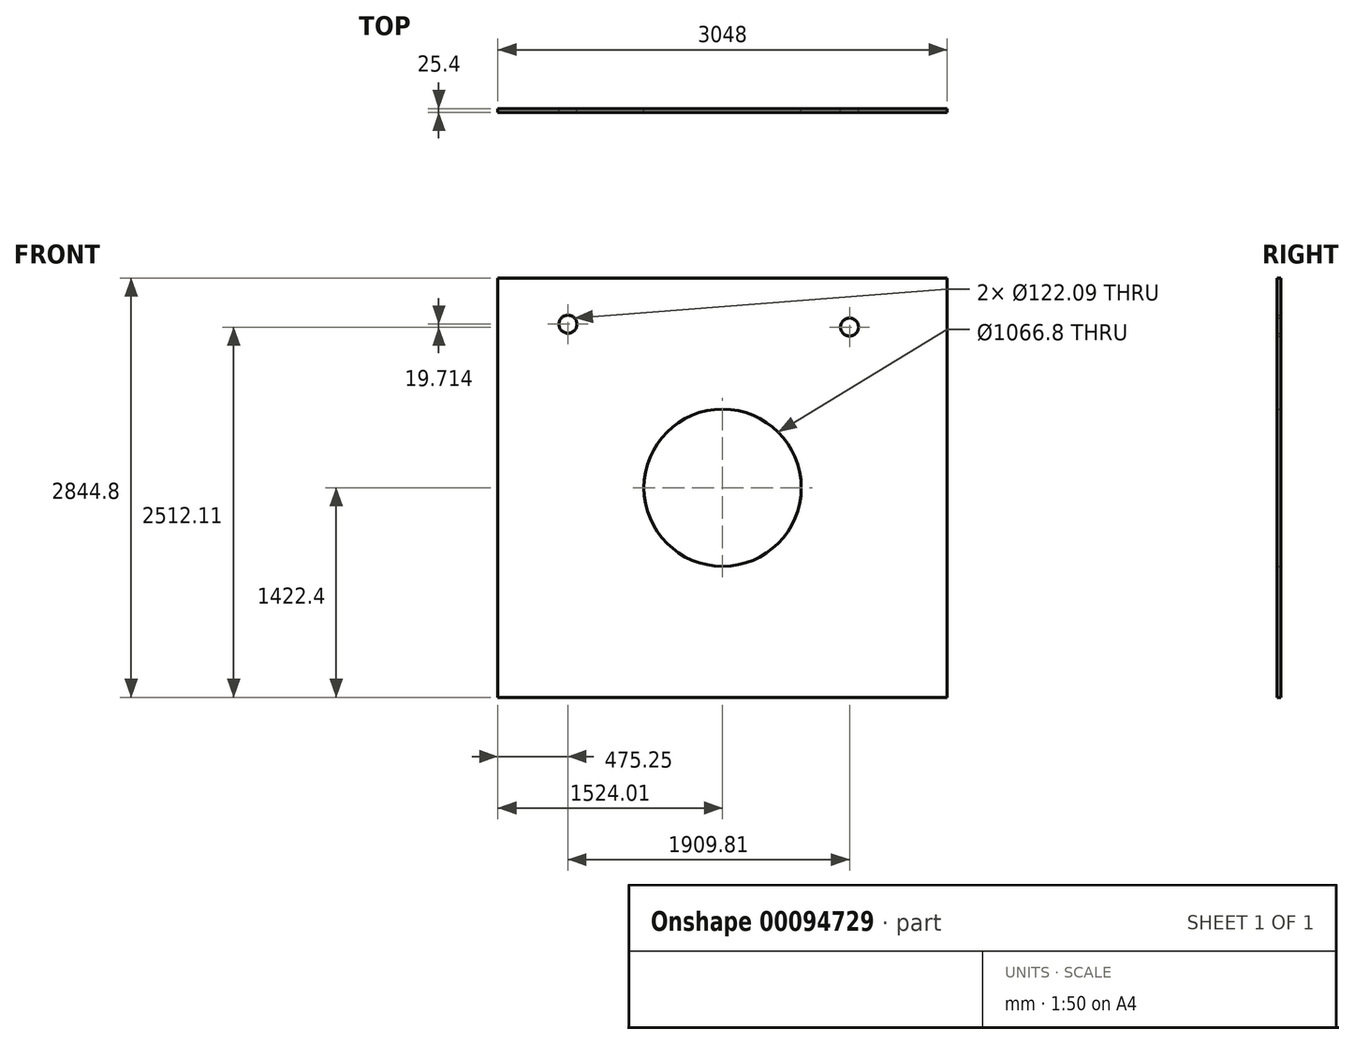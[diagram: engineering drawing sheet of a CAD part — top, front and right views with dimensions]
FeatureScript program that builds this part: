
annotation { "Feature Type Name" : "Feature", "Feature Type Description" : "" }
export const myFeature = defineFeature(function(context is Context, id is Id, definition is map)
    precondition{}
    {
        {
            var Q0;
            Q0=qCreatedBy(makeId("Front.planeOp"),FACE);
            var sketch = newSketch(context, id + "F0", { "sketchPlane" : qUnion([Q0])});
            skLineSegment(sketch, "E0.bottom", {"start": v(-1748.58, 0) * mm, "end": v(1299.42, 0) * mm});
            skLineSegment(sketch, "E0.top", {"start": v(-1748.58, 2844.8) * mm, "end": v(1299.42, 2844.8) * mm});
            skLineSegment(sketch, "E0.left", {"start": v(-1748.58, 0) * mm, "end": v(-1748.58, 2844.8) * mm});
            skLineSegment(sketch, "E0.right", {"start": v(1299.42, 0) * mm, "end": v(1299.42, 2844.8) * mm});
            skCircle(sketch, "E1", {"center": v(-224.58, 1422.4) * mm, "radius": 533.4 * mm});
            skPoint(sketch, "E1.centerSnap0", {"position": v(1299.42, 1422.4) * mm});
            skPoint(sketch, "E1.centerSnap1", {"position": v(-224.58, 0) * mm});
            skCircle(sketch, "E2", {"center": v(-1273.33, 2531.83) * mm, "radius": 61.04 * mm});
            skCircle(sketch, "E3", {"center": v(636.48, 2512.11) * mm, "radius": 61.04 * mm});
            skSolve(sketch);
        }
        {
            var Q0;
            Q0=makeQuery(id+"F0.imprint","IMPRINT",FACE,{"disambiguationData":[TD([[makeQuery(id+"F0.imprint","IMPRINT",EDGE,{"derivedFrom":sQuery(id+"F0.wireOp",EDGE,"E0.bottom")}),1.0]])]});
            extrude(context, id + "F1", {"entities" : qUnion([Q0]), "depth" : 25.4 * mm});
        }
    });
